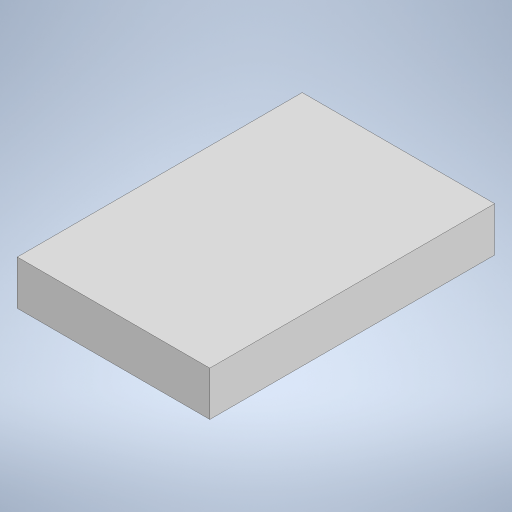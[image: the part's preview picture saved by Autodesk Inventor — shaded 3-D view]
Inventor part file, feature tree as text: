
AUTODESK INVENTOR PART (.ipt)
format: ipt  version: 2023 (Build 270158000, 158)  size: 189,952 bytes
history: native  units: mm
features: extrude x1, sketch x1
ambient origin geometry x8: Origin, YZ Plane, XZ Plane, XY Plane, X Axis, Y Axis, Z Axis, Center Point
bodies: Solid1 (feature_tree)
feature tree (2):
  extrude  "Extrusion1"  Depth=0.64mm
  sketch  "Sketch1"  dims[d0=2.77mm d1=0.64mm d2=4.1mm d3=0.0mm]
